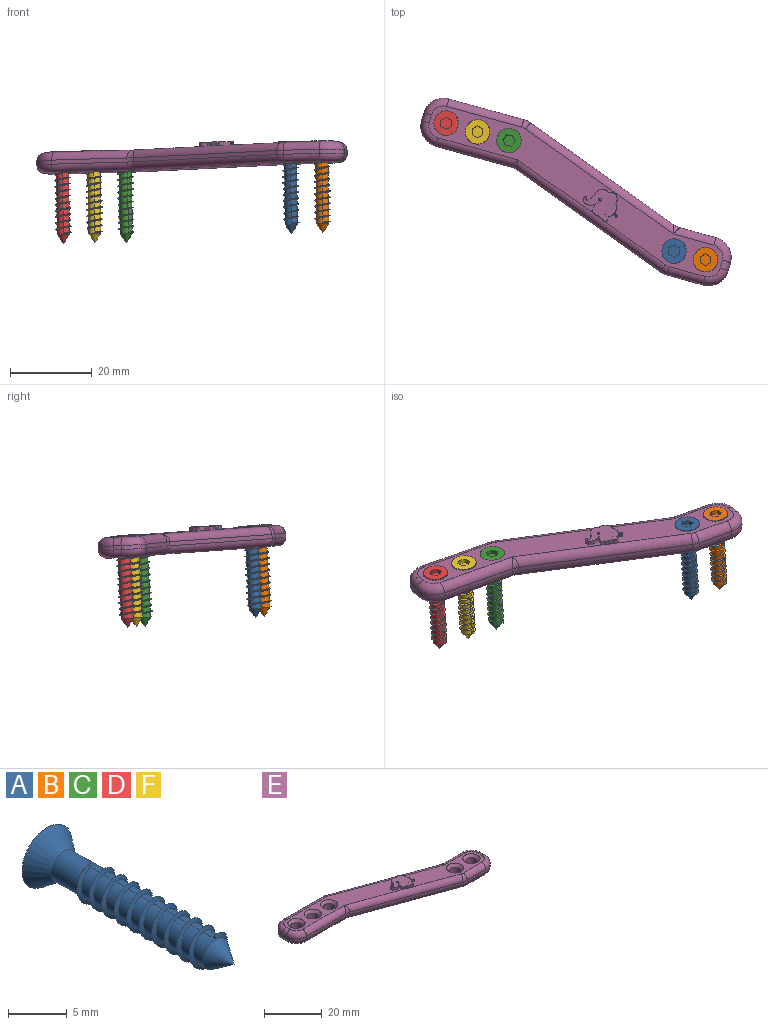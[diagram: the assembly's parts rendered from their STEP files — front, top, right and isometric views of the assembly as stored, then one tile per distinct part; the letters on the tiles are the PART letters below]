
ASSEMBLY  parts=6 mates=5
PART A: 25 faces, bbox 6x22.5x6 mm
  f0: plane 6x6mm, normal (0,1,0), area 22.4mm2, adj f1,f18,f19,f20,f21,f22,f23
  f1: cone r=3mm half-angle=36.9deg, axis (0,1,0), area 35.3mm2, adj f0,f2
  f2: cylinder r=1.5mm len=4.5mm, axis (0,1,0), area 35.3mm2, adj f1,f3,f13,f15
  f3: cylinder r=1.5mm len=3mm, axis (0,1,0), area 11.3mm2, adj f2,f4,f15,f16
  f4: cylinder r=1.5mm len=3mm, axis (0,1,0), area 11.3mm2, adj f3,f5,f15,f16
  f5: cylinder r=1.5mm len=3mm, axis (0,1,0), area 11.3mm2, adj f4,f6,f15,f16
  f6: cylinder r=1.5mm len=3mm, axis (0,1,0), area 11.3mm2, adj f5,f7,f15,f16
  f7: cylinder r=1.5mm len=3mm, axis (0,1,0), area 11.3mm2, adj f6,f8,f15,f16
  f8: cylinder r=1.5mm len=3mm, axis (0,1,0), area 11.3mm2, adj f7,f9,f15,f16
  f9: cylinder r=1.5mm len=3mm, axis (0,1,0), area 11.3mm2, adj f8,f10,f15,f16
  f10: cylinder r=1.5mm len=3mm, axis (0,1,0), area 11.3mm2, adj f9,f11,f15,f16
  f11: cylinder r=1.5mm len=3mm, axis (0,1,0), area 11.3mm2, adj f10,f12,f15,f16
  f12: cylinder r=1.5mm len=3mm, axis (0,1,0), area 7.1mm2, adj f11,f14,f16,f17
  f13: plane 0.4x0.3mm, normal (1,0,0), area 0.1mm2, adj f2,f15,f16
  f14: plane 0.4x0.3mm, normal (-1,0,0), area 0.1mm2, adj f12,f15,f16
  f15: bspline ~15.15x4.39mm, area 46mm2, adj f2,f3,f4,f5,f6,f7,f8,f9
  f16: bspline ~15.15x4.39mm, area 45.9mm2, adj f3,f4,f5,f6,f7,f8,f9,f10
  f17: cone r=1.5mm half-angle=34.3deg, axis (0,1,0), area 12.5mm2, adj f12
  f18: plane 1.5x1mm, normal (1,0,0), area 1.5mm2, adj f0,f19,f23,f24
  f19: plane 1.3x1mm, normal (0.5,0,-0.87), area 1.5mm2, adj f0,f18,f20,f24
  f20: plane 1.3x1mm, normal (-0.5,0,-0.87), area 1.5mm2, adj f0,f19,f21,f24
  f21: plane 1.5x1mm, normal (-1,0,0), area 1.5mm2, adj f0,f20,f22,f24
  f22: plane 1.3x1mm, normal (-0.5,0,0.87), area 1.5mm2, adj f0,f21,f23,f24
  f23: plane 1.3x1mm, normal (0.5,0,0.87), area 1.5mm2, adj f0,f18,f22,f24
  f24: plane 3x2.6mm, normal (0,1,0), area 5.8mm2, adj f18,f19,f20,f21,f22,f23
PART B: same geometry as A
PART C: same geometry as A
PART D: same geometry as A
PART E: 81 faces, bbox 83.1x28.2x6 mm
  f0: plane 1.93x0.74mm, normal (0,0,1), area 0.3mm2, adj f24,f67,f68,f69
  f1: plane 78.29x23.39mm, normal (0,0,1), area 427.5mm2, adj f24,f25,f26,f27,f28,f29,f30,f31
  f2: plane 78.29x23.39mm, normal (0,0,-1), area 544.8mm2, adj f11,f12,f13,f14,f15,f16,f17,f18
  f3: plane 40.63x14.79mm, normal (0.34,0.94,0), area 43.2mm2, adj f18,f31,f48,f54
  f4: plane 19.12x1mm, normal (0,1,0), area 19.1mm2, adj f16,f29,f45,f48
  f5: plane 2x1mm, normal (-1,0,0), area 2mm2, adj f17,f27,f42,f45
  f6: plane 19.12x1mm, normal (0,-1,0), area 19.1mm2, adj f19,f25,f42,f51
  f7: plane 40.63x14.79mm, normal (-0.34,-0.94,0), area 43.2mm2, adj f21,f24,f36,f51
  f8: plane 9.12x1mm, normal (0,-1,0), area 9.1mm2, adj f23,f26,f33,f36
  f9: plane 2x1mm, normal (1,0,0), area 2mm2, adj f22,f28,f33,f39
  f10: plane 9.12x1mm, normal (0,1,0), area 9.1mm2, adj f20,f30,f39,f54
  f11: cylinder r=2mm len=4mm, axis (0,0,1), area 50.3mm2, adj f2,f58
  f12: cylinder r=2mm len=4mm, axis (0,0,1), area 50.3mm2, adj f2,f59
  f13: cylinder r=2mm len=4mm, axis (0,0,1), area 50.3mm2, adj f2,f60
  f14: cylinder r=2mm len=4mm, axis (0,0,1), area 50.3mm2, adj f2,f57
  f15: cylinder r=2mm len=4mm, axis (0,0,1), area 50.3mm2, adj f2,f56
  f16: cylinder r=2mm len=19.12mm, axis (-1,0,0), area 60.1mm2, adj f2,f4,f46,f49
  f17: cylinder r=2mm len=2mm, axis (0,-1,0), area 6.3mm2, adj f2,f5,f43,f46
  f18: cylinder r=2mm len=42.47mm, axis (-0.94,0.34,0), area 137.2mm2, adj f2,f3,f49,f53
  f19: cylinder r=2mm len=20.35mm, axis (1,0,0), area 61.5mm2, adj f2,f6,f43,f50
  f20: cylinder r=2mm len=10.35mm, axis (-1,0,0), area 30.1mm2, adj f2,f10,f40,f53
  f21: cylinder r=2mm len=42.47mm, axis (0.94,-0.34,0), area 137.2mm2, adj f2,f7,f37,f50
  f22: cylinder r=2mm len=2mm, axis (0,1,0), area 6.3mm2, adj f2,f9,f34,f40
  f23: cylinder r=2mm len=9.12mm, axis (1,0,0), area 28.6mm2, adj f2,f8,f34,f37
  f24: cylinder r=2mm len=42.47mm, axis (-0.94,0.34,0), area 137.2mm2, adj f0,f1,f7,f35,f52,f61,f66
  f25: cylinder r=2mm len=20.35mm, axis (-1,0,0), area 61.5mm2, adj f1,f6,f41,f52
  f26: cylinder r=2mm len=9.12mm, axis (-1,0,0), area 28.6mm2, adj f1,f8,f32,f35
  f27: cylinder r=2mm len=2mm, axis (0,1,0), area 6.3mm2, adj f1,f5,f41,f44
  f28: cylinder r=2mm len=2mm, axis (0,-1,0), area 6.3mm2, adj f1,f9,f32,f38
  f29: cylinder r=2mm len=19.12mm, axis (1,0,0), area 60.1mm2, adj f1,f4,f44,f47
  f30: cylinder r=2mm len=10.35mm, axis (1,0,0), area 30.1mm2, adj f1,f10,f38,f55
  f31: cylinder r=2mm len=42.47mm, axis (0.94,-0.34,0), area 137.2mm2, adj f1,f3,f47,f55
  f32: torus R=3mm, axis (0,0,1), area 21.1mm2, adj f1,f26,f28,f33
  f33: cylinder r=5mm len=5mm, axis (0,0,1), area 7.9mm2, adj f8,f9,f32,f34
  f34: torus R=3mm, axis (0,0,1), area 21.1mm2, adj f2,f22,f23,f33
  f35: torus R=3mm, axis (0,0,1), area 4.7mm2, adj f1,f24,f26,f36
  f36: cylinder r=5mm len=1.71mm, axis (0,0,-1), area 1.7mm2, adj f7,f8,f35,f37
  f37: torus R=3mm, axis (0,0,1), area 4.7mm2, adj f2,f21,f23,f36
  f38: torus R=3mm, axis (0,0,1), area 21.1mm2, adj f1,f28,f30,f39
  f39: cylinder r=5mm len=5mm, axis (0,0,-1), area 7.9mm2, adj f9,f10,f38,f40
  f40: torus R=3mm, axis (0,0,1), area 21.1mm2, adj f2,f20,f22,f39
  f41: torus R=3mm, axis (0,0,1), area 21.1mm2, adj f1,f25,f27,f42
  f42: cylinder r=5mm len=5mm, axis (0,0,1), area 7.9mm2, adj f5,f6,f41,f43
  f43: torus R=3mm, axis (0,0,1), area 21.1mm2, adj f2,f17,f19,f42
  f44: torus R=3mm, axis (0,0,1), area 21.1mm2, adj f1,f27,f29,f45
  f45: cylinder r=5mm len=5mm, axis (0,0,-1), area 7.9mm2, adj f4,f5,f44,f46
  f46: torus R=3mm, axis (0,0,1), area 21.1mm2, adj f2,f16,f17,f45
  f47: torus R=3mm, axis (0,0,1), area 4.7mm2, adj f1,f29,f31,f48
  f48: cylinder r=5mm len=1.71mm, axis (0,0,-1), area 1.7mm2, adj f3,f4,f47,f49
  f49: torus R=3mm, axis (0,0,1), area 4.7mm2, adj f2,f16,f18,f48
  f50: bspline ~2.3x2.26mm, area 3.5mm2, adj f19,f21,f51
  f51: cylinder r=5mm len=1.71mm, axis (0,0,1), area 1.7mm2, adj f6,f7,f50,f52
  f52: bspline ~2.3x2.26mm, area 3.5mm2, adj f24,f25,f51
  f53: bspline ~2.3x2.26mm, area 3.5mm2, adj f18,f20,f54
  f54: cylinder r=5mm len=1.71mm, axis (0,0,1), area 1.7mm2, adj f3,f10,f53,f55
  f55: bspline ~2.3x2.26mm, area 3.5mm2, adj f30,f31,f54
  f56: cone r=2mm half-angle=45deg, axis (0,0,1), area 22.2mm2, adj f1,f15
  f57: cone r=2mm half-angle=45deg, axis (0,0,1), area 22.2mm2, adj f1,f14
  f58: cone r=2mm half-angle=45deg, axis (0,0,1), area 22.2mm2, adj f1,f11
  f59: cone r=2mm half-angle=45deg, axis (0,0,1), area 22.2mm2, adj f1,f12
  f60: cone r=2mm half-angle=45deg, axis (0,0,1), area 22.2mm2, adj f1,f13
  f61: plane 0.43x0.17mm, normal (0,0,-1), area 0mm2, adj f24,f69
  f62: extruded ~1x0.01mm, area 0mm2, adj f73,f77,f79
  f63: extruded ~1x0.12mm, area 0.1mm2, adj f74,f77,f78
  f64: extruded ~2.19x1mm, area 2.8mm2, adj f1,f65,f75,f77
  f65: extruded ~1x0.53mm, area 0.6mm2, adj f1,f64,f66,f77
  f66: plane 1x0.02mm, normal (-0.34,-0.94,0), area 0mm2, adj f24,f65,f67,f77
  f67: extruded ~1x0.48mm, area 0.5mm2, adj f0,f66,f68,f77
  f68: extruded ~1.11x1mm, area 1.2mm2, adj f0,f67,f69,f77
  f69: extruded ~2.58x2.56mm, area 4.3mm2, adj f0,f1,f61,f68,f70,f77
  f70: extruded ~1x0.97mm, area 3.1mm2, adj f1,f69,f71,f77
  f71: extruded ~2.27x1mm, area 2.4mm2, adj f1,f70,f72,f77
  f72: extruded ~7.54x3.67mm, area 11.9mm2, adj f1,f71,f75,f77
  f73: extruded ~1x0.22mm, area 0.5mm2, adj f62,f77,f79
  f74: extruded ~1x0.12mm, area 0.1mm2, adj f63,f77,f78
  f75: extruded ~3.13x1.9mm, area 5.2mm2, adj f1,f64,f72,f77
  f76: cylinder r=0.35mm len=1mm, axis (0,0,-1), area 2.2mm2, adj f77,f80
  f77: plane 9.17x7.54mm, normal (0,0,1), area 38.4mm2, adj f62,f63,f64,f65,f66,f67,f68,f69
  f78: plane 0.13x0.03mm, normal (0,0,1), area 0mm2, adj f63,f74
  f79: plane 0.25x0.18mm, normal (0,0,1), area 0mm2, adj f62,f73
  f80: plane 0.69x0.69mm, normal (0,0,1), area 0.4mm2, adj f76
PART F: same geometry as A
PLACE A rot(axis=(1,-0.01,0.01),87.2deg) t=(68.76,14.38,-1.41)mm
PLACE B rot(axis=(1,-0.01,0.01),87.2deg) t=(76.47,12.25,-1.19)mm
PLACE C rot(axis=(0.97,0.17,0.18),88.9deg) t=(28.27,41.49,-3.63)mm
PLACE D rot(axis=(1,-0.01,0.01),87.2deg) t=(12.85,45.75,-3.82)mm
PLACE E rot(axis=(-0.17,-0.08,-0.98),15.7deg) t=(5.54,41.31,-8.98)mm
PLACE F rot(axis=(1,-0.01,0.01),87.2deg) t=(20.55,43.63,-3.6)mm
MATE cylindrical D.f1 <-> E.f13  axis (-0.02,0.05,1) through (12.88,45.65,-5.82)mm
MATE cylindrical B.f1 <-> E.f15  axis (-0.02,0.05,1) through (76.5,12.15,-3.19)mm
MATE cylindrical F.f1 <-> E.f12  axis (-0.02,0.05,1) through (20.59,43.53,-5.59)mm
MATE cylindrical A.f1 <-> E.f14  axis (-0.02,0.05,1) through (68.79,14.28,-3.41)mm
MATE cylindrical C.f1 <-> E.f11  axis (-0.02,0.05,1) through (28.3,41.39,-5.63)mm
